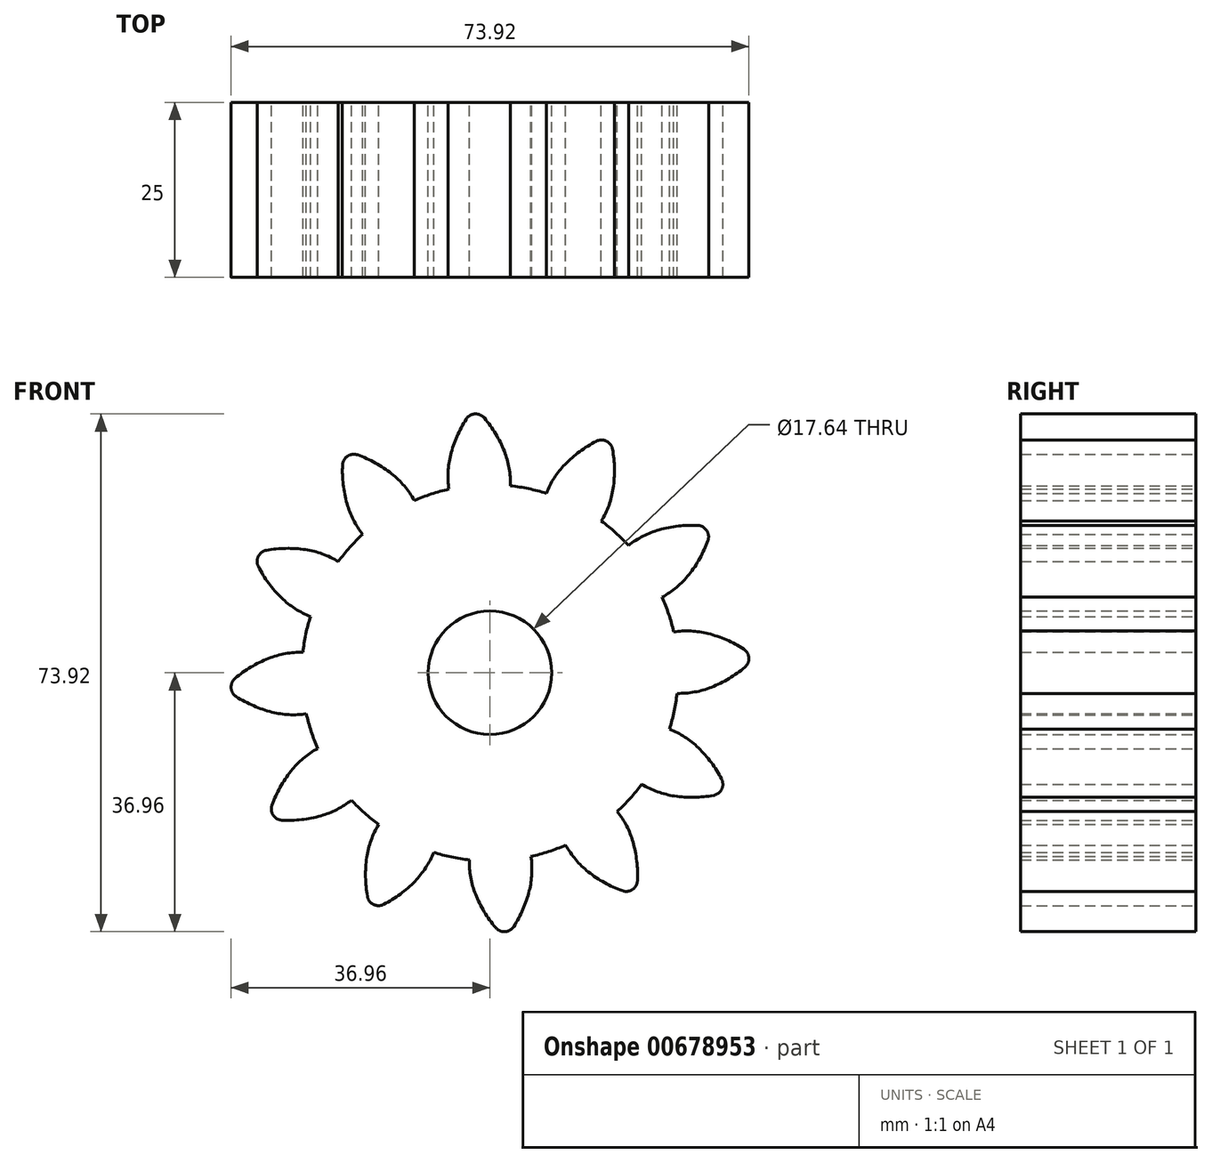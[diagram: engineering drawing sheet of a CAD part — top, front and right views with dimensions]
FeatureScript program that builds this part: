
annotation { "Feature Type Name" : "Feature", "Feature Type Description" : "" }
export const myFeature = defineFeature(function(context is Context, id is Id, definition is map)
    precondition{}
    {
        {
            var Q0;
            Q0=qCreatedBy(makeId("Front.planeOp"),FACE);
            var sketch = newSketch(context, id + "F0", { "sketchPlane" : qUnion([Q0])});
            skCircle(sketch, "E0", {"center": v(0, 0) * mm, "radius": 26.86 * mm});
            skCircle(sketch, "E1", {"center": v(0, 0) * mm, "radius": 29.34 * mm, "construction": true});
            skCircle(sketch, "E2", {"center": v(0, 0) * mm, "radius": 31.75 * mm, "construction": true});
            skLineSegment(sketch, "E3", {"start": v(0, 29.34) * mm, "end": v(-76.8, 29.34) * mm, "construction": true});
            skLineSegment(sketch, "E4", {"start": v(0, 29.34) * mm, "end": v(-72.34, 3) * mm, "construction": true});
            skCircle(sketch, "E5", {"center": v(0, 29.34) * mm, "radius": 7.3 * mm, "construction": true});
            skCircle(sketch, "E6", {"center": v(0, 0) * mm, "radius": 27.57 * mm, "construction": true});
            skCircle(sketch, "E7", {"center": v(-6.86, 26.84) * mm, "radius": 7.3 * mm, "construction": true});
            skArc(sketch, "E8", {"start": v(2.05, 31.62) * mm, "mid": v(0.82, 34.12) * mm, "end": v(-0.8, 36.39) * mm});
            skArc(sketch, "E9", {"start": v(2.93, 26.66) * mm, "mid": v(2.75, 29.19) * mm, "end": v(2.05, 31.62) * mm});
            skArc(sketch, "E10.MirrorCS", {"start": v(-5.6, 31.12) * mm, "mid": v(-4.7, 33.76) * mm, "end": v(-3.4, 36.22) * mm});
            skArc(sketch, "E11.MirrorCS", {"start": v(-5.83, 26.09) * mm, "mid": v(-5.98, 28.62) * mm, "end": v(-5.6, 31.12) * mm});
            skArc(sketch, "E12", {"start": v(-0.8, 36.39) * mm, "mid": v(-2.14, 36.96) * mm, "end": v(-3.4, 36.22) * mm});
            skCircle(sketch, "E13", {"center": v(0, 0) * mm, "radius": 8.82 * mm});
            skSolve(sketch);
        }
        {
            var Q0;
            {var subQ0=sQuery(id+"F0.wireOp",EDGE,"E0");var subQ1=makeQuery(id+"F0.imprint","INTERSECT",VERTEX,{"derivedFrom":[subQ0,sQuery(id+"F0.wireOp",EDGE,"w2nq9C5J-QsR5-B1Ja-DJJq-NUCfvcJc4RYo")]});Q0=makeQuery(id+"F0.imprint","IMPRINT",FACE,{"disambiguationData":[TD([[makeQuery(id+"F0.imprint","IMPRINT",EDGE,{"disambiguationData":[TD([[subQ1,-1.0]])],"derivedFrom":subQ0}),1.0]])]});}
            var Q1;
            Q1=makeQuery(id+"F0.imprint","IMPRINT",FACE,{"disambiguationData":[TD([[makeQuery(id+"F0.imprint","IMPRINT",EDGE,{"derivedFrom":sQuery(id+"F0.wireOp",EDGE,"rFtHzzam-Afbj-mfBk-tnUL-QJqSVwKd1ZrJ")}),1.0]])]});
            var Q2;
            {var subQ2=sQuery(id+"F0.wireOp",EDGE,"E8");Q2=makeQuery(id+"F0.imprint","IMPRINT",FACE,{"disambiguationData":[TD([[makeQuery(id+"F0.imprint","IMPRINT",EDGE,{"derivedFrom":subQ2}),1.0]])]});}
            extrude(context, id + "F1", {"entities" : qUnion([Q0, Q1, Q2]), "depth" : 25 * mm, "offsetDistance" : 25 * mm});
        }
        {
            var Q0;
            Q0=makeQuery(id+"F1.opExtrude","SWEPT_BODY",BODY,{"disambiguationData":[OSD([sQuery(id+"F0.wireOp",EDGE,"E0"),sQuery(id+"F0.wireOp",EDGE,"rFtHzzam-Afbj-mfBk-tnUL-QJqSVwKd1ZrJ"),sQuery(id+"F0.wireOp",EDGE,"w2nq9C5J-QsR5-B1Ja-DJJq-NUCfvcJc4RYo"),sQuery(id+"F0.wireOp",EDGE,"06e9aee6-cd32-42ea-9868-1e50b7951aff0.MirrorCS"),sQuery(id+"F0.wireOp",EDGE,"83598d93-3ebf-4dd3-854a-4ef60b7524d90.MirrorCS"),sQuery(id+"F0.wireOp",EDGE,"M6qhRUna-RuDn-7AWu-aOg9-8YzQ2V54zNsk")])]});
            var Q1;
            Q1=makeQuery(id+"F1.opExtrude","SWEPT_FACE",FACE,{"disambiguationData":[OSD([sQuery(id+"F0.wireOp",EDGE,"E0")])]});
            circularPattern(context, id + "F2", {"operationType" : NewBodyOperationType.ADD, "entities" : qUnion([Q0]), "axis" : qUnion([Q1]), "angle" : 360 * degree, "instanceCount" : 12, "equalSpace" : true});
        }
    });
